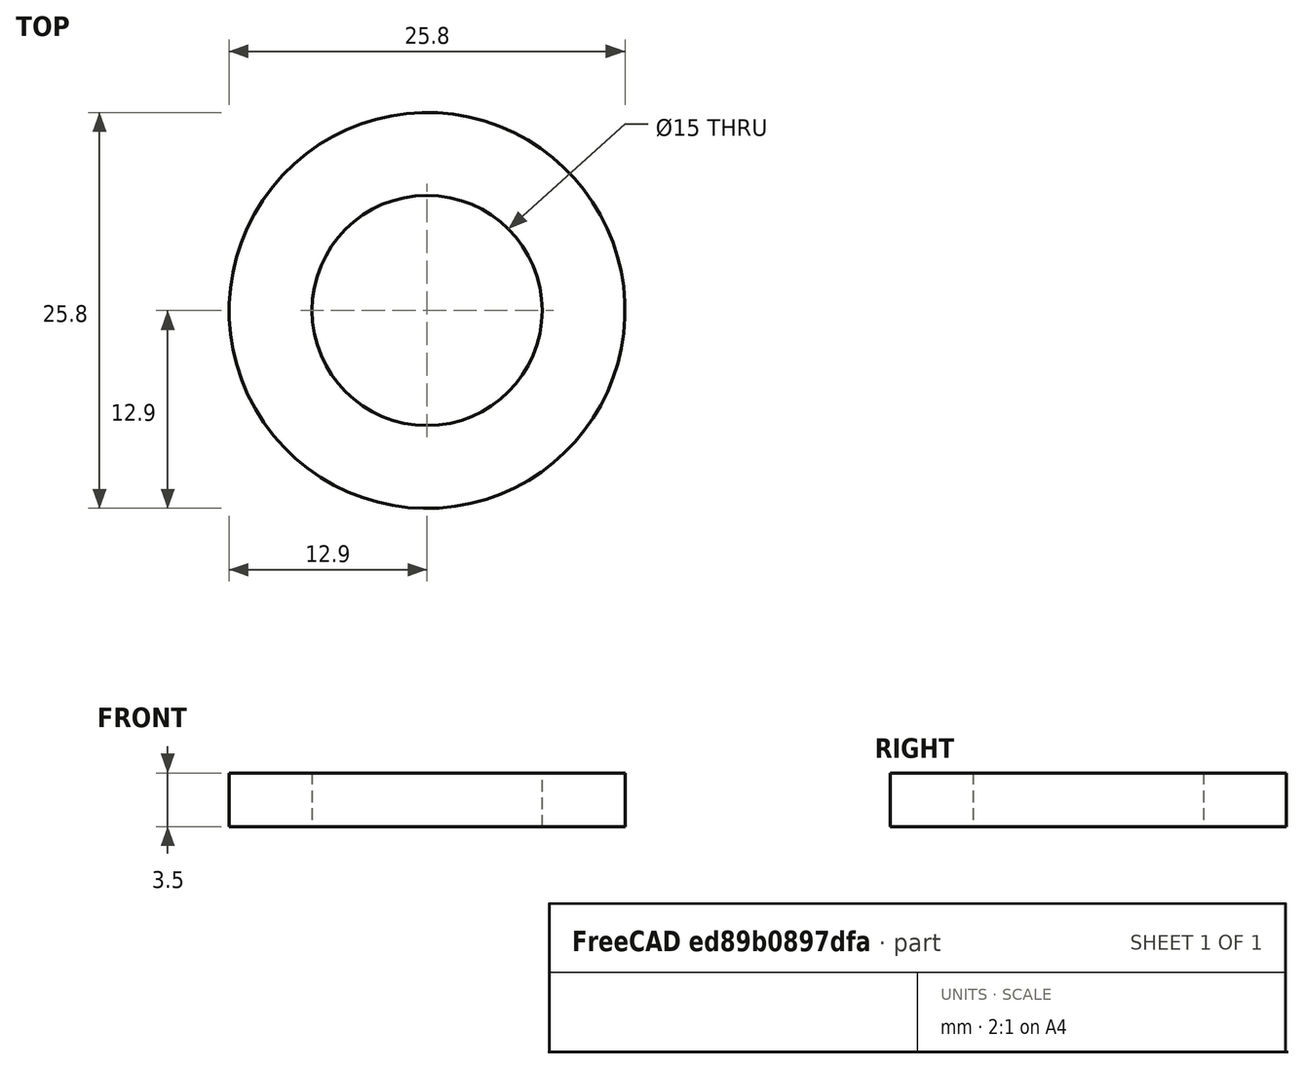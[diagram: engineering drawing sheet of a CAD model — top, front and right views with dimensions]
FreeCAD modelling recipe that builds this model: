
FCSTD DOCUMENT  (FreeCAD 0.16R)
Label: CrankSpacer3.5mmround
License: All rights reserved
LicenseURL: http://en.wikipedia.org/wiki/All_rights_reserved
objects: Sketcher::SketchObject×1, PartDesign::Pad×1, Mesh::Feature×1
note: 3 computed .brp shape members not serialized (recipe doc carries the construction recipe); baked Part::Feature solids carry a one-line shape summary decoded from their .brp

FEATURE [Sketcher::SketchObject] Sketch
  sketch-geometry (3):
    g0: Circle CenterX=0 CenterY=0 CenterZ=0 NormalX=0 NormalY=0 NormalZ=1 Radius=7.5
    g1: ArcOfCircle CenterX=0 CenterY=0 CenterZ=0 NormalX=0 NormalY=0 NormalZ=1 Radius=12.8994 StartAngle=1.19516 EndAngle=5.01635
    g2: ArcOfCircle CenterX=0 CenterY=0 CenterZ=0 NormalX=0 NormalY=0 NormalZ=1 Radius=12.8994 StartAngle=5.01635 EndAngle=7.47835
  constraints (8):
    c: Coincident(g0,g-1)
    c: Radius(g0) = 7.5
    c: Equal(g1,g2)
    c: Coincident(g1,g-1)
    c: DistanceY(g1) = 12
    c: Coincident(g2,g1)
    c: Coincident(g2,g1)
    c: Coincident(g2,g-1)
FEATURE [PartDesign::Pad] Pad
  Length = 3.5
  Length2 = 100
  Sketch = -> Sketch
  Type = 0
FEATURE [Mesh::Feature] Mesh  label="Pad (Meshed)"
